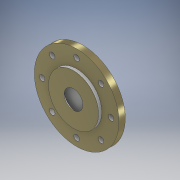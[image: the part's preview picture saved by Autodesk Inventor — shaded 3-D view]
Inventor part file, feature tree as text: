
AUTODESK INVENTOR PART (.ipt)
format: ipt  version: 2017 (Build 210142000, 142)  size: 183,296 bytes
history: native  units: mm
features: extrude x4, sketch x3, fillet x2, chamfer x1
ambient origin geometry x8: Origin, YZ Plane, XZ Plane, XY Plane, X Axis, Y Axis, Z Axis, Center Point
bodies: Solid1 (feature_tree)
feature tree (10):
  sketch  "Sketch1"  dims[d1=80.0mm d2=54.0mm d3=32.0mm d4=44.0mm d5=3.5mm d6=360.0deg d7=22.0mm d8=22.0mm]
  extrude  "Extrusion1"  Depth=22.0mm
  extrude  "Extrusion2"  Depth=2.0mm TaperAngle=0.0deg
  extrude  "Extrusion3"  Depth=5.0mm TaperAngle=0.0deg
  extrude  "Extrusion4"  Depth=2.0mm
  fillet  "Fillet1"  Radius=15.0mm
  fillet  "Fillet2"  [1 undecoded]
  chamfer  "Chamfer1"  Distance=1.0mm
  sketch  "Sketch2"  dims[d9=4.0mm d10=0.0mm d11=2.0mm d12=0.0mm]
  sketch  "Sketch3"  dims[d13=12.0mm d14=0.0mm d15=5.0mm d16=0.0mm d17=30.0mm d18=15.0mm d19=0.0mm d20=0.0mm d21=1.0mm d22=15.0mm d23=2.0mm d24=2.0mm d25=45.0deg]
note: 1 required parameter value undecoded (feature->parameter linkage not recoverable at this tier; creation-order binding heuristic only, values carry confidence <= 0.55)
